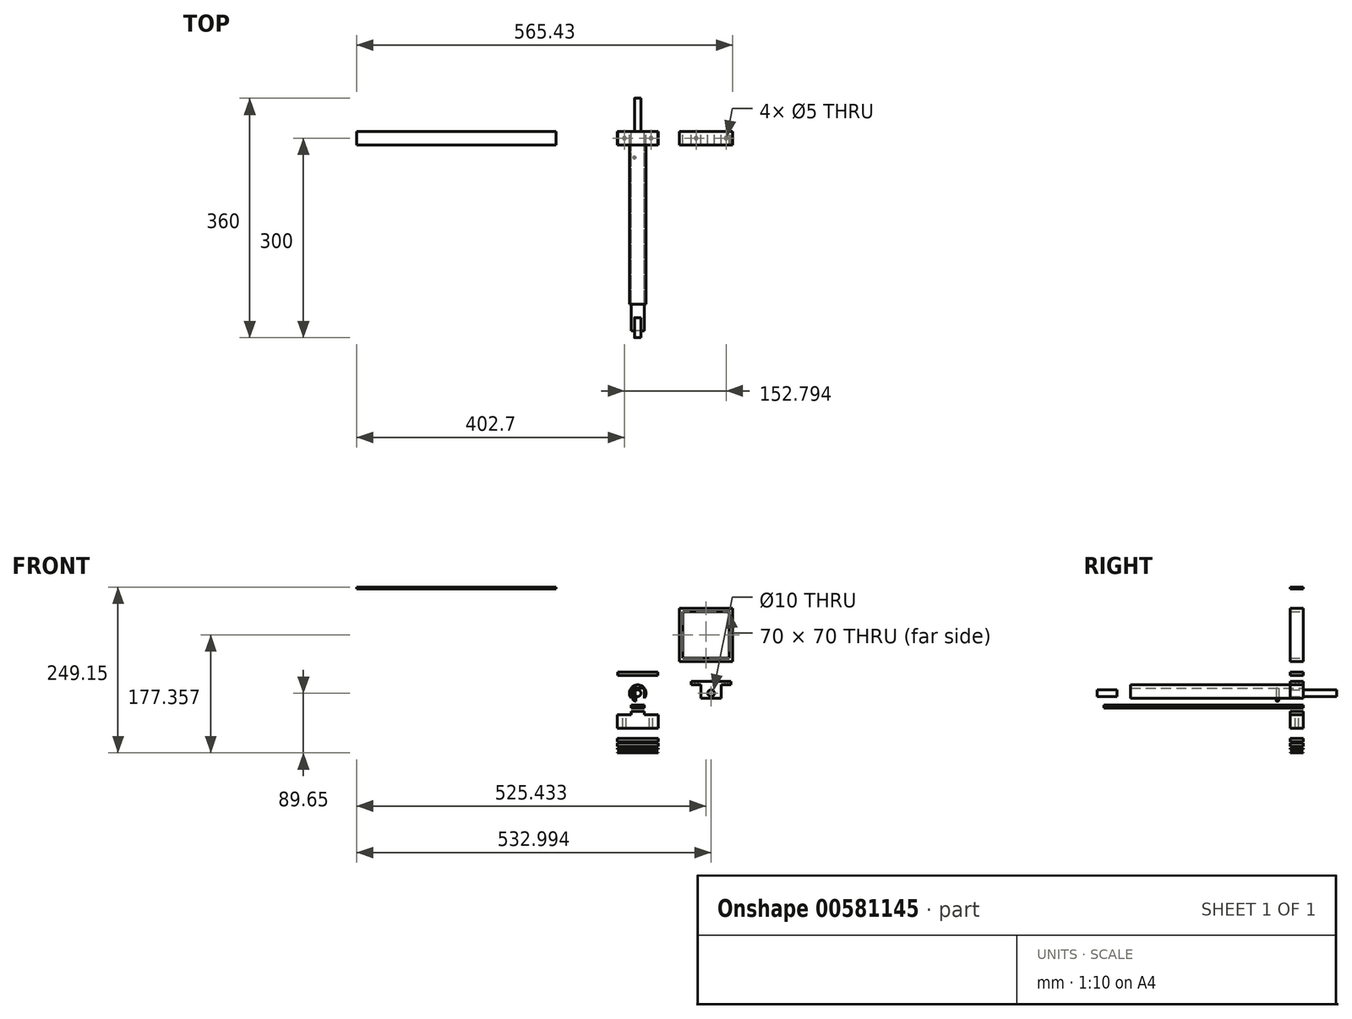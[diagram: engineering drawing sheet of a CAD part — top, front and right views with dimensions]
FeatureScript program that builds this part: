
annotation { "Feature Type Name" : "Feature", "Feature Type Description" : "" }
export const myFeature = defineFeature(function(context is Context, id is Id, definition is map)
    precondition{}
    {
        {
            var Q0;
            Q0=qCreatedBy(makeId("Front.planeOp"),FACE);
            var sketch = newSketch(context, id + "F0", { "sketchPlane" : qUnion([Q0])});
            skCircle(sketch, "E0", {"center": v(0, 0) * mm, "radius": 12.5 * mm});
            skCircle(sketch, "E1", {"center": v(110.3, 0) * mm, "radius": 5 * mm});
            skLineSegment(sketch, "E2.bottom", {"start": v(-30, 31.74) * mm, "end": v(30, 31.74) * mm});
            skLineSegment(sketch, "E2.top", {"start": v(-30, 26.74) * mm, "end": v(30, 26.74) * mm});
            skLineSegment(sketch, "E2.left", {"start": v(-30, 31.74) * mm, "end": v(-30, 26.74) * mm});
            skLineSegment(sketch, "E2.right", {"start": v(30, 31.74) * mm, "end": v(30, 26.74) * mm});
            skPoint(sketch, "E2.middle", {"position": v(0, 29.24) * mm});
            skLineSegment(sketch, "E3", {"start": v(110.3, 10) * mm, "end": v(110.3, -10) * mm, "construction": true});
            skCircle(sketch, "E4", {"center": v(110.3, 0) * mm, "radius": 12.5 * mm, "construction": true});
            skLineSegment(sketch, "E5", {"start": v(97.8, 0) * mm, "end": v(122.8, 0) * mm, "construction": true});
            skLineSegment(sketch, "E6", {"start": v(110.3, 12.5) * mm, "end": v(79.29, 12.5) * mm, "construction": true});
            skLineSegment(sketch, "E7", {"start": v(110.3, 5) * mm, "end": v(79.29, 5) * mm, "construction": true});
            skLineSegment(sketch, "E8", {"start": v(110.3, -5) * mm, "end": v(79.29, -5) * mm, "construction": true});
            skLineSegment(sketch, "E9", {"start": v(110.3, -12.5) * mm, "end": v(79.29, -12.5) * mm, "construction": true});
            skLineSegment(sketch, "E10", {"start": v(110.3, -7.5) * mm, "end": v(125.3, -7.5) * mm});
            skLineSegment(sketch, "E11", {"start": v(110.3, 17.5) * mm, "end": v(140.3, 17.5) * mm});
            skLineSegment(sketch, "E12", {"start": v(125.3, 12.5) * mm, "end": v(140.3, 12.5) * mm});
            skLineSegment(sketch, "E13", {"start": v(125.3, -7.5) * mm, "end": v(125.3, 12.5) * mm});
            skLineSegment(sketch, "E14", {"start": v(140.3, 17.5) * mm, "end": v(140.3, 12.5) * mm});
            skPoint(sketch, "E15.orphan", {"position": v(110.3, 12.5) * mm});
            skLineSegment(sketch, "E16.MirrorCS", {"start": v(95.3, 12.5) * mm, "end": v(80.3, 12.5) * mm});
            skLineSegment(sketch, "E17.MirrorCS", {"start": v(80.3, 17.5) * mm, "end": v(80.3, 12.5) * mm});
            skLineSegment(sketch, "E18.MirrorCS", {"start": v(110.3, 17.5) * mm, "end": v(80.3, 17.5) * mm});
            skLineSegment(sketch, "E19.MirrorCS", {"start": v(95.3, -7.5) * mm, "end": v(95.3, 12.5) * mm});
            skLineSegment(sketch, "E20.MirrorCS", {"start": v(110.3, -7.5) * mm, "end": v(95.3, -7.5) * mm});
            skLineSegment(sketch, "E21.top", {"start": v(0, -27.58) * mm, "end": v(10, -27.58) * mm});
            skLineSegment(sketch, "E22", {"start": v(10.93, -32.58) * mm, "end": v(30.93, -32.58) * mm});
            skLineSegment(sketch, "E23", {"start": v(30.93, -32.58) * mm, "end": v(30.93, -52.58) * mm});
            skLineSegment(sketch, "E24", {"start": v(30.93, -52.58) * mm, "end": v(0, -52.58) * mm});
            skLineSegment(sketch, "E25.MirrorCS", {"start": v(0, -27.58) * mm, "end": v(-10, -27.58) * mm});
            skLineSegment(sketch, "E26.MirrorCS", {"start": v(-10.93, -32.58) * mm, "end": v(-30.93, -32.58) * mm});
            skLineSegment(sketch, "E27.MirrorCS", {"start": v(-30.93, -32.58) * mm, "end": v(-30.93, -52.58) * mm});
            skLineSegment(sketch, "E28.MirrorCS", {"start": v(-30.93, -52.58) * mm, "end": v(0, -52.58) * mm});
            skLineSegment(sketch, "E29", {"start": v(0, -22.52) * mm, "end": v(10, -22.52) * mm});
            skLineSegment(sketch, "E30", {"start": v(10, -22.52) * mm, "end": v(10, -17.52) * mm});
            skLineSegment(sketch, "E31", {"start": v(10, -17.52) * mm, "end": v(0, -17.52) * mm});
            skLineSegment(sketch, "E32.MirrorCS", {"start": v(-10, -17.52) * mm, "end": v(0, -17.52) * mm});
            skLineSegment(sketch, "E33.MirrorCS", {"start": v(0, -22.52) * mm, "end": v(-10, -22.52) * mm});
            skLineSegment(sketch, "E34.MirrorCS", {"start": v(-10, -22.52) * mm, "end": v(-10, -17.52) * mm});
            skLineSegment(sketch, "E35.bottom", {"start": v(137.73, 52.7) * mm, "end": v(67.73, 52.7) * mm});
            skLineSegment(sketch, "E35.top", {"start": v(137.73, 122.7) * mm, "end": v(67.73, 122.7) * mm});
            skLineSegment(sketch, "E35.left", {"start": v(137.73, 52.7) * mm, "end": v(137.73, 122.7) * mm});
            skLineSegment(sketch, "E35.right", {"start": v(67.73, 52.7) * mm, "end": v(67.73, 122.7) * mm});
            skPoint(sketch, "E35.middle", {"position": v(102.73, 87.7) * mm});
            skLineSegment(sketch, "E36.bottom", {"start": v(62.73, 127.7) * mm, "end": v(142.73, 127.7) * mm});
            skLineSegment(sketch, "E36.top", {"start": v(62.73, 47.7) * mm, "end": v(142.73, 47.7) * mm});
            skLineSegment(sketch, "E36.left", {"start": v(62.73, 127.7) * mm, "end": v(62.73, 47.7) * mm});
            skLineSegment(sketch, "E36.right", {"start": v(142.73, 127.7) * mm, "end": v(142.73, 47.7) * mm});
            skLineSegment(sketch, "E37.bottom", {"start": v(-30.93, -79.86) * mm, "end": v(30.93, -79.86) * mm});
            skLineSegment(sketch, "E37.top", {"start": v(-30.93, -74.86) * mm, "end": v(30.93, -74.86) * mm});
            skLineSegment(sketch, "E37.left", {"start": v(-30.93, -79.86) * mm, "end": v(-30.93, -74.86) * mm});
            skLineSegment(sketch, "E37.right", {"start": v(30.93, -79.86) * mm, "end": v(30.93, -74.86) * mm});
            skLineSegment(sketch, "E38.MirrorCS", {"start": v(-30.74, -88.65) * mm, "end": v(31.12, -88.65) * mm});
            skLineSegment(sketch, "E39.MirrorCS", {"start": v(-30.74, -89.65) * mm, "end": v(31.12, -89.65) * mm});
            skLineSegment(sketch, "E40", {"start": v(-30.93, -82.76) * mm, "end": v(30.93, -82.76) * mm});
            skLineSegment(sketch, "E41", {"start": v(30.93, -82.76) * mm, "end": v(30.93, -84.76) * mm});
            skLineSegment(sketch, "E42", {"start": v(30.93, -84.76) * mm, "end": v(-30.93, -84.76) * mm});
            skLineSegment(sketch, "E43", {"start": v(-30.93, -84.76) * mm, "end": v(-30.93, -82.76) * mm});
            skLineSegment(sketch, "E44", {"start": v(-30.74, -88.65) * mm, "end": v(-30.74, -89.65) * mm});
            skLineSegment(sketch, "E45", {"start": v(31.12, -88.65) * mm, "end": v(31.12, -89.65) * mm});
            skLineSegment(sketch, "E46", {"start": v(-30.93, -72.74) * mm, "end": v(30.93, -72.74) * mm});
            skLineSegment(sketch, "E47", {"start": v(30.93, -72.74) * mm, "end": v(30.93, -67.74) * mm});
            skLineSegment(sketch, "E48", {"start": v(30.93, -67.74) * mm, "end": v(-30.93, -67.74) * mm});
            skLineSegment(sketch, "E49", {"start": v(-30.93, -67.74) * mm, "end": v(-30.93, -72.74) * mm});
            skLineSegment(sketch, "E50", {"start": v(-10, -27.58) * mm, "end": v(-10, -32.58) * mm});
            skLineSegment(sketch, "E51", {"start": v(-10, -32.58) * mm, "end": v(-10.93, -32.58) * mm});
            skPoint(sketch, "E52.MirrorCS.end.orphan", {"position": v(-10, -27.58) * mm});
            skPoint(sketch, "E52.MirrorCS.start.orphan", {"position": v(-10.93, -32.58) * mm});
            skLineSegment(sketch, "E53", {"start": v(10, -27.58) * mm, "end": v(10, -32.58) * mm});
            skLineSegment(sketch, "E54", {"start": v(10, -32.58) * mm, "end": v(10.93, -32.58) * mm});
            skLineSegment(sketch, "E55.left", {"start": v(194.47, 95.4) * mm, "end": v(194.47, 97.9) * mm});
            skLineSegment(sketch, "E56.bottom", {"start": v(-122.7, 157) * mm, "end": v(-422.7, 157) * mm});
            skLineSegment(sketch, "E56.top", {"start": v(-122.7, 159.5) * mm, "end": v(-422.7, 159.5) * mm});
            skLineSegment(sketch, "E56.left", {"start": v(-122.7, 157) * mm, "end": v(-122.7, 159.5) * mm});
            skLineSegment(sketch, "E56.right", {"start": v(-422.7, 157) * mm, "end": v(-422.7, 159.5) * mm});
            skSolve(sketch);
        }
        {
            var Q0;
            Q0=makeQuery(id+"F0.imprint","IMPRINT",FACE,{"disambiguationData":[TD([[makeQuery(id+"F0.imprint","IMPRINT",EDGE,{"derivedFrom":sQuery(id+"F0.wireOp",EDGE,"E1")}),-1.0]])]});
            var Q1;
            Q1=makeQuery(id+"F0.imprint","IMPRINT",FACE,{"disambiguationData":[TD([[makeQuery(id+"F0.imprint","IMPRINT",EDGE,{"derivedFrom":sQuery(id+"F0.wireOp",EDGE,"E2.bottom")}),-1.0]])]});
            var Q2;
            Q2=makeQuery(id+"F0.imprint","IMPRINT",FACE,{"disambiguationData":[TD([[makeQuery(id+"F0.imprint","IMPRINT",EDGE,{"derivedFrom":sQuery(id+"F0.wireOp",EDGE,"E21.top")}),-1.0]])]});
            var Q3;
            Q3=makeQuery(id+"F0.imprint","IMPRINT",FACE,{"disambiguationData":[TD([[makeQuery(id+"F0.imprint","IMPRINT",EDGE,{"derivedFrom":sQuery(id+"F0.wireOp",EDGE,"E35.bottom")}),1.0]])]});
            var Q4;
            Q4=makeQuery(id+"F0.imprint","IMPRINT",FACE,{"disambiguationData":[TD([[makeQuery(id+"F0.imprint","IMPRINT",EDGE,{"derivedFrom":sQuery(id+"F0.wireOp",EDGE,"E37.bottom")}),1.0]])]});
            var Q5;
            Q5=makeQuery(id+"F0.imprint","IMPRINT",FACE,{"disambiguationData":[TD([[makeQuery(id+"F0.imprint","IMPRINT",EDGE,{"derivedFrom":sQuery(id+"F0.wireOp",EDGE,"E38.MirrorCS")}),-1.0]])]});
            var Q6;
            Q6=makeQuery(id+"F0.imprint","IMPRINT",FACE,{"disambiguationData":[TD([[makeQuery(id+"F0.imprint","IMPRINT",EDGE,{"derivedFrom":sQuery(id+"F0.wireOp",EDGE,"E40")}),-1.0]])]});
            var Q7;
            Q7=makeQuery(id+"F0.imprint","IMPRINT",FACE,{"disambiguationData":[TD([[makeQuery(id+"F0.imprint","IMPRINT",EDGE,{"derivedFrom":sQuery(id+"F0.wireOp",EDGE,"E46")}),1.0]])]});
            var Q8;
            {var subQ5=sQuery(id+"F0.wireOp",EDGE,"E55.right");Q8=makeQuery(id+"F0.imprint","IMPRINT",FACE,{"disambiguationData":[TD([[makeQuery(id+"F0.imprint","IMPRINT",EDGE,{"derivedFrom":subQ5}),-1.0]])]});}
            var Q9;
            Q9=makeQuery(id+"F0.imprint","IMPRINT",FACE,{"disambiguationData":[TD([[makeQuery(id+"F0.imprint","IMPRINT",EDGE,{"derivedFrom":sQuery(id+"F0.wireOp",EDGE,"E56.bottom")}),-1.0]])]});
            extrude(context, id + "F1", {"entities" : qUnion([Q0, Q1, Q2, Q3, Q4, Q5, Q6, Q7, Q8, Q9]), "depth" : 20 * mm, "offsetDistance" : 25 * mm});
        }
        {
            var Q0;
            Q0=makeQuery(id+"F0.imprint","IMPRINT",FACE,{"disambiguationData":[TD([[makeQuery(id+"F0.imprint","IMPRINT",EDGE,{"derivedFrom":sQuery(id+"F0.wireOp",EDGE,"E0")}),1.0]])]});
            extrude(context, id + "F2", {"entities" : qUnion([Q0]), "depth" : 260 * mm, "offsetDistance" : 25 * mm});
        }
        {
            var Q0;
            Q0=makeQuery(id+"F2.opExtrude","CAP_FACE",FACE,{"disambiguationData":[OSD([sQuery(id+"F0.wireOp",EDGE,"E0")])],"isStart":false});
            var sketch = newSketch(context, id + "F3", { "sketchPlane" : qUnion([Q0])});
            skCircle(sketch, "E57", {"center": v(0, 0) * mm, "radius": 5 * mm});
            skSolve(sketch);
        }
        {
            var Q0;
            Q0=makeQuery(id+"F3.imprint","IMPRINT",FACE,{"disambiguationData":[TD([[makeQuery(id+"F3.imprint","IMPRINT",EDGE,{"derivedFrom":sQuery(id+"F3.wireOp",EDGE,"E57")}),1.0]])]});
            extrude(context, id + "F4", {"entities" : qUnion([Q0]), "operationType" : NewBodyOperationType.ADD, "depth" : 50 * mm, "offsetDistance" : 25 * mm});
        }
        {
            var Q0;
            Q0=makeQuery(id+"F0.imprint","IMPRINT",FACE,{"disambiguationData":[TD([[makeQuery(id+"F0.imprint","IMPRINT",EDGE,{"derivedFrom":sQuery(id+"F0.wireOp",EDGE,"E29")}),1.0]])]});
            extrude(context, id + "F5", {"entities" : qUnion([Q0]), "depth" : 300 * mm, "offsetDistance" : 25 * mm});
        }
        {
            var Q0;
            Q0=makeQuery(id+"F1.opExtrude","SWEPT_FACE",FACE,{"disambiguationData":[OSD([sQuery(id+"F0.wireOp",EDGE,"E26.MirrorCS")])]});
            var sketch = newSketch(context, id + "F6", { "sketchPlane" : qUnion([Q0])});
            skCircle(sketch, "E58", {"center": v(-20, -10) * mm, "radius": 2.5 * mm});
            skSolve(sketch);
        }
        {
            var Q0;
            Q0=makeQuery(id+"F1.opExtrude","SWEPT_FACE",FACE,{"disambiguationData":[OSD([sQuery(id+"F0.wireOp",EDGE,"E22")])]});
            var sketch = newSketch(context, id + "F7", { "sketchPlane" : qUnion([Q0])});
            skCircle(sketch, "E59", {"center": v(20, -10) * mm, "radius": 2.5 * mm});
            skSolve(sketch);
        }
        {
            var Q0;
            Q0=makeQuery(id+"F6.imprint","IMPRINT",FACE,{"disambiguationData":[TD([[makeQuery(id+"F6.imprint","IMPRINT",EDGE,{"derivedFrom":sQuery(id+"F6.wireOp",EDGE,"E58")}),1.0]])]});
            var Q1;
            Q1=makeQuery(id+"F7.imprint","IMPRINT",FACE,{"disambiguationData":[TD([[makeQuery(id+"F7.imprint","IMPRINT",EDGE,{"derivedFrom":sQuery(id+"F7.wireOp",EDGE,"E59")}),1.0]])]});
            extrude(context, id + "F8", {"entities" : qUnion([Q0, Q1]), "operationType" : NewBodyOperationType.REMOVE, "oppositeDirection" : true, "depth" : 25 * mm, "offsetDistance" : 25 * mm});
        }
        {
            var Q0;
            Q0=makeQuery(id+"F1.opExtrude","SWEPT_FACE",FACE,{"disambiguationData":[OSD([sQuery(id+"F0.wireOp",EDGE,"E12")])]});
            var sketch = newSketch(context, id + "F9", { "sketchPlane" : qUnion([Q0])});
            skCircle(sketch, "E60", {"center": v(132.8, 10) * mm, "radius": 2.5 * mm});
            skPoint(sketch, "E60.centerSnap0", {"position": v(132.8, 20) * mm});
            skPoint(sketch, "E60.centerSnap1", {"position": v(125.3, 10) * mm});
            skSolve(sketch);
        }
        {
            var Q0;
            Q0=makeQuery(id+"F1.opExtrude","SWEPT_FACE",FACE,{"disambiguationData":[OSD([sQuery(id+"F0.wireOp",EDGE,"E16.MirrorCS")])]});
            var sketch = newSketch(context, id + "F10", { "sketchPlane" : qUnion([Q0])});
            skCircle(sketch, "E61", {"center": v(87.8, 10) * mm, "radius": 2.5 * mm});
            skPoint(sketch, "E61.centerSnap0", {"position": v(80.3, 10) * mm});
            skPoint(sketch, "E61.centerSnap1", {"position": v(87.8, 20) * mm});
            skSolve(sketch);
        }
        {
            var Q0;
            Q0=makeQuery(id+"F10.imprint","IMPRINT",FACE,{"disambiguationData":[TD([[makeQuery(id+"F10.imprint","IMPRINT",EDGE,{"derivedFrom":sQuery(id+"F10.wireOp",EDGE,"E61")}),1.0]])]});
            var Q1;
            Q1=makeQuery(id+"F9.imprint","IMPRINT",FACE,{"disambiguationData":[TD([[makeQuery(id+"F9.imprint","IMPRINT",EDGE,{"derivedFrom":sQuery(id+"F9.wireOp",EDGE,"E60")}),1.0]])]});
            extrude(context, id + "F11", {"entities" : qUnion([Q0, Q1]), "operationType" : NewBodyOperationType.REMOVE, "oppositeDirection" : true, "depth" : 25 * mm, "offsetDistance" : 25 * mm});
        }
        {
            var Q0;
            Q0=makeQuery(id+"F5.opExtrude","SWEPT_FACE",FACE,{"disambiguationData":[OSD([sQuery(id+"F0.wireOp",EDGE,"E31"),sQuery(id+"F0.wireOp",EDGE,"E32.MirrorCS")])]});
            var sketch = newSketch(context, id + "F12", { "sketchPlane" : qUnion([Q0])});
            skLineSegment(sketch, "E62", {"start": v(-10, -280) * mm, "end": v(10, -280) * mm});
            skCircle(sketch, "E63", {"center": v(5, -39.13) * mm, "radius": 1.93 * mm});
            skPoint(sketch, "E64.orphan", {"position": v(0, -300) * mm});
            skCircle(sketch, "E65.MirrorC", {"center": v(-5, -39.13) * mm, "radius": 1.93 * mm});
            skSolve(sketch);
        }
        {
            var Q0;
            Q0=makeQuery(id+"F12.imprint","IMPRINT",FACE,{"disambiguationData":[TD([[makeQuery(id+"F12.imprint","IMPRINT",EDGE,{"derivedFrom":sQuery(id+"F12.wireOp",EDGE,"E65.MirrorC")}),-1.0]])]});
            var Q1;
            Q1=makeQuery(id+"F12.imprint","IMPRINT",FACE,{"disambiguationData":[TD([[makeQuery(id+"F12.imprint","IMPRINT",EDGE,{"derivedFrom":sQuery(id+"F12.wireOp",EDGE,"E63")}),1.0]])]});
            extrude(context, id + "F13", {"entities" : qUnion([Q0, Q1]), "operationType" : NewBodyOperationType.REMOVE, "depth" : 25 * mm, "offsetDistance" : 25 * mm});
        }
        {
            var Q0;
            Q0=makeQuery(id+"F1.opExtrude","SWEPT_FACE",FACE,{"disambiguationData":[OSD([sQuery(id+"F0.wireOp",EDGE,"E56.bottom")])]});
            var sketch = newSketch(context, id + "F14", { "sketchPlane" : qUnion([Q0])});
            skLineSegment(sketch, "E66", {"start": v(-402.7, 0) * mm, "end": v(-402.7, 20) * mm});
            skLineSegment(sketch, "E67", {"start": v(-142.7, 0) * mm, "end": v(-142.7, 20) * mm});
            skLineSegment(sketch, "E68", {"start": v(82.73, 0) * mm, "end": v(82.73, 20) * mm});
            skLineSegment(sketch, "E69", {"start": v(122.73, 0) * mm, "end": v(122.73, 20) * mm});
            skSolve(sketch);
        }
        {
            var Q0;
            Q0=makeQuery(id+"F1.opExtrude","SWEPT_FACE",FACE,{"disambiguationData":[OSD([sQuery(id+"F0.wireOp",EDGE,"E36.bottom")])]});
            var sketch = newSketch(context, id + "F15", { "sketchPlane" : qUnion([Q0])});
            skLineSegment(sketch, "E70", {"start": v(82.73, 0) * mm, "end": v(82.73, -20) * mm});
            skLineSegment(sketch, "E71", {"start": v(122.73, -20) * mm, "end": v(122.73, 0) * mm});
            skSolve(sketch);
        }
        {
            var Q0;
            Q0=makeQuery(id+"F1.opExtrude","SWEPT_FACE",FACE,{"disambiguationData":[OSD([sQuery(id+"F0.wireOp",EDGE,"E36.top")])]});
            var sketch = newSketch(context, id + "F16", { "sketchPlane" : qUnion([Q0])});
            skLineSegment(sketch, "E72", {"start": v(122.73, 20) * mm, "end": v(122.73, 0) * mm});
            skLineSegment(sketch, "E73", {"start": v(82.73, 20) * mm, "end": v(82.73, 0) * mm});
            skSolve(sketch);
        }
        {
            var Q0;
            Q0=makeQuery(id+"F2.opExtrude","CAP_FACE",FACE,{"disambiguationData":[OSD([sQuery(id+"F0.wireOp",EDGE,"E0")])],"isStart":true});
            var sketch = newSketch(context, id + "F17", { "sketchPlane" : qUnion([Q0])});
            skCircle(sketch, "E74", {"center": v(0, 0) * mm, "radius": 5 * mm});
            skSolve(sketch);
        }
        {
            var Q0;
            Q0 = qSketchRegion(id + "F17", true);
            extrude(context, id + "F18", {"entities" : qUnion([Q0]), "operationType" : NewBodyOperationType.ADD, "depth" : 50 * mm, "offsetDistance" : 25 * mm});
        }
    });
